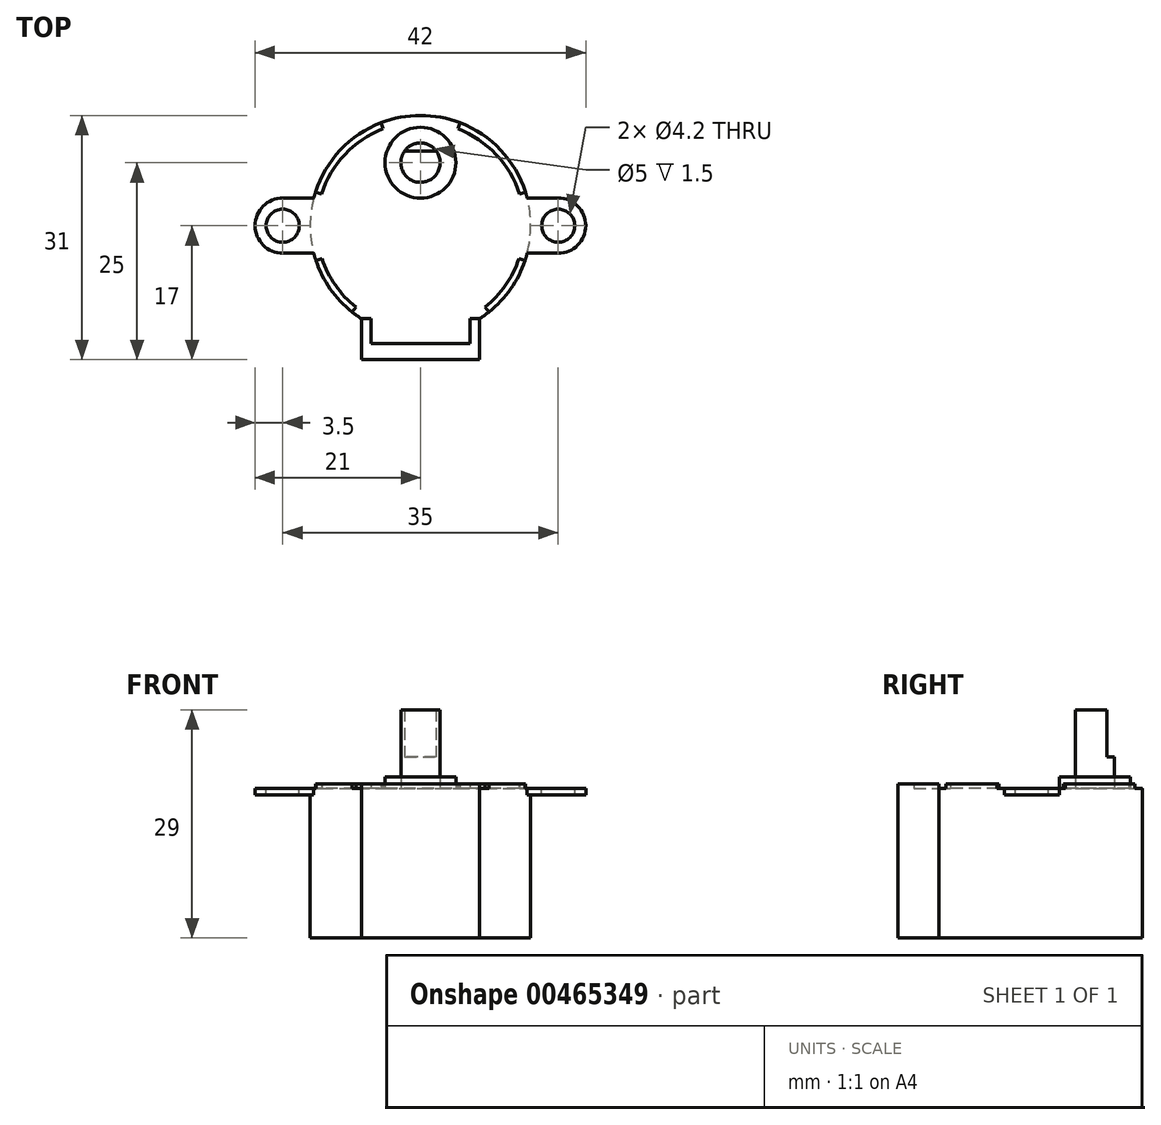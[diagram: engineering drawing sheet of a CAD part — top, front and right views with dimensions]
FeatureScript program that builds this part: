
annotation { "Feature Type Name" : "Feature", "Feature Type Description" : "" }
export const myFeature = defineFeature(function(context is Context, id is Id, definition is map)
    precondition{}
    {
        {
            var Q0;
            Q0=qCreatedBy(makeId("Top.planeOp"),FACE);
            var sketch = newSketch(context, id + "F0", { "sketchPlane" : qUnion([Q0])});
            skArc(sketch, "E0", {"start": v(7.5, -11.82) * mm, "mid": v(0, 14) * mm, "end": v(-7.5, -11.82) * mm});
            skCircle(sketch, "E1", {"center": v(-17.5, 0) * mm, "radius": 2.1 * mm});
            skCircle(sketch, "E2", {"center": v(17.5, 0) * mm, "radius": 2.1 * mm});
            skCircle(sketch, "E3", {"center": v(0, 8) * mm, "radius": 4.5 * mm});
            skArc(sketch, "E4", {"start": v(17.5, -3.5) * mm, "mid": v(21, 0) * mm, "end": v(17.5, 3.5) * mm});
            skArc(sketch, "E5", {"start": v(-17.5, 3.5) * mm, "mid": v(-21, 0) * mm, "end": v(-17.5, -3.5) * mm});
            skLineSegment(sketch, "E6", {"start": v(17.5, -3.5) * mm, "end": v(13.56, -3.5) * mm});
            skLineSegment(sketch, "E7", {"start": v(-17.5, 3.5) * mm, "end": v(-13.56, 3.5) * mm});
            skLineSegment(sketch, "E8.rect.bottom", {"start": v(7.5, -17) * mm, "end": v(-7.5, -17) * mm});
            skLineSegment(sketch, "E8.rect.left", {"start": v(7.5, -17) * mm, "end": v(7.5, -11.82) * mm});
            skLineSegment(sketch, "E8.rect.right", {"start": v(-7.5, -17) * mm, "end": v(-7.5, -11.82) * mm});
            skPoint(sketch, "E9.orphan", {"position": v(-7.5, 17) * mm});
            skPoint(sketch, "E10.orphan", {"position": v(7.5, 17) * mm});
            skLineSegment(sketch, "E11.trimOffspring", {"start": v(13.56, 3.5) * mm, "end": v(17.5, 3.5) * mm});
            skLineSegment(sketch, "E12.trimOffspring", {"start": v(-13.56, -3.5) * mm, "end": v(-17.5, -3.5) * mm});
            skCircle(sketch, "E13", {"center": v(0, 8) * mm, "radius": 2.5 * mm});
            skSolve(sketch);
        }
        {
            var Q0;
            Q0=makeQuery(id+"F0.imprint","IMPRINT",FACE,{"disambiguationData":[TD([[makeQuery(id+"F0.imprint","IMPRINT",EDGE,{"derivedFrom":sQuery(id+"F0.wireOp",EDGE,"E3")}),-1.0]])]});
            var Q1;
            Q1=makeQuery(id+"F0.imprint","IMPRINT",FACE,{"disambiguationData":[TD([[makeQuery(id+"F0.imprint","IMPRINT",EDGE,{"derivedFrom":sQuery(id+"F0.wireOp",EDGE,"E3")}),1.0]])]});
            var Q2;
            Q2=makeQuery(id+"F0.imprint","IMPRINT",FACE,{"disambiguationData":[TD([[makeQuery(id+"F0.imprint","IMPRINT",EDGE,{"derivedFrom":sQuery(id+"F0.wireOp",EDGE,"E13")}),1.0]])]});
            extrude(context, id + "F1", {"entities" : qUnion([Q0, Q1, Q2]), "depth" : 19 * mm});
        }
        {
            var Q0;
            Q0=makeQuery(id+"F0.imprint","IMPRINT",FACE,{"disambiguationData":[TD([[makeQuery(id+"F0.imprint","IMPRINT",EDGE,{"derivedFrom":sQuery(id+"F0.wireOp",EDGE,"E1")}),-1.0]])]});
            var Q1;
            Q1=makeQuery(id+"F0.imprint","IMPRINT",FACE,{"disambiguationData":[TD([[makeQuery(id+"F0.imprint","IMPRINT",EDGE,{"derivedFrom":sQuery(id+"F0.wireOp",EDGE,"E2")}),-1.0]])]});
            extrude(context, id + "F2", {"entities" : qUnion([Q0, Q1]), "operationType" : NewBodyOperationType.ADD, "depth" : 0.8 * mm});
        }
        {
            var Q0;
            Q0=makeQuery(id+"F0.imprint","IMPRINT",FACE,{"disambiguationData":[TD([[makeQuery(id+"F0.imprint","IMPRINT",EDGE,{"derivedFrom":sQuery(id+"F0.wireOp",EDGE,"E3")}),1.0]])]});
            extrude(context, id + "F3", {"entities" : qUnion([Q0]), "operationType" : NewBodyOperationType.ADD, "oppositeDirection" : true, "depth" : 1.5 * mm});
        }
        {
            var Q0;
            Q0=makeQuery(id+"F0.imprint","IMPRINT",FACE,{"disambiguationData":[TD([[makeQuery(id+"F0.imprint","IMPRINT",EDGE,{"derivedFrom":sQuery(id+"F0.wireOp",EDGE,"E13")}),1.0]])]});
            extrude(context, id + "F4", {"entities" : qUnion([Q0]), "oppositeDirection" : true, "depth" : 10 * mm});
        }
        {
            var Q0;
            Q0=makeQuery(id+"F4.opExtrude","CAP_FACE",FACE,{"disambiguationData":[OSD([sQuery(id+"F0.wireOp",EDGE,"E13")])],"isStart":false});
            var sketch = newSketch(context, id + "F5", { "sketchPlane" : qUnion([Q0])});
            skLineSegment(sketch, "E14.rect.bottom", {"start": v(2.91, -9.5) * mm, "end": v(-2.91, -9.5) * mm});
            skLineSegment(sketch, "E14.rect.top", {"start": v(2.91, -6.5) * mm, "end": v(-2.91, -6.5) * mm});
            skLineSegment(sketch, "E14.rect.left", {"start": v(2.91, -9.5) * mm, "end": v(2.91, -6.5) * mm});
            skLineSegment(sketch, "E14.rect.right", {"start": v(-2.91, -9.5) * mm, "end": v(-2.91, -6.5) * mm});
            skPoint(sketch, "E14.rect.middle", {"position": v(0, -8) * mm});
            skLineSegment(sketch, "E15.bottom", {"start": v(-2.91, -6.5) * mm, "end": v(2.91, -6.5) * mm});
            skLineSegment(sketch, "E15.top", {"start": v(-2.91, -5.02) * mm, "end": v(2.91, -5.02) * mm});
            skLineSegment(sketch, "E15.left", {"start": v(-2.91, -6.5) * mm, "end": v(-2.91, -5.02) * mm});
            skLineSegment(sketch, "E15.right", {"start": v(2.91, -6.5) * mm, "end": v(2.91, -5.02) * mm});
            skLineSegment(sketch, "E16.top", {"start": v(2.91, -10.83) * mm, "end": v(-2.91, -10.83) * mm});
            skLineSegment(sketch, "E16.left", {"start": v(2.91, -9.5) * mm, "end": v(2.91, -10.83) * mm});
            skLineSegment(sketch, "E16.right", {"start": v(-2.91, -9.5) * mm, "end": v(-2.91, -10.83) * mm});
            skSolve(sketch);
        }
        {
            var Q0;
            Q0=makeQuery(id+"F5.imprint","IMPRINT",FACE,{"disambiguationData":[TD([[makeQuery(id+"F5.imprint","IMPRINT",EDGE,{"derivedFrom":sQuery(id+"F5.wireOp",EDGE,"E15.top")}),-1.0]])]});
            var Q1;
            {var subQ0=makeQuery(id+"F4.opExtrude","CAP_EDGE",EDGE,{"disambiguationData":[OSD([sQuery(id+"F0.wireOp",EDGE,"E13")])],"isStart":false});var subQ1=sQuery(id+"F5.wireOp",EDGE,"E15.bottom");var subQ3=makeQuery(id+"F5.imprint","INTERSECT",VERTEX,{"disambiguationData":[OD(0.0)],"derivedFrom":[subQ0,subQ1]});Q1=makeQuery(id+"F5.imprint","IMPRINT",FACE,{"disambiguationData":[TD([[makeQuery(id+"F5.imprint","IMPRINT",EDGE,{"disambiguationData":[TD([[subQ3,-1.0]])],"derivedFrom":subQ1}),1.0]])]});}
            var Q2;
            {var subQ0=makeQuery(id+"F4.opExtrude","CAP_EDGE",EDGE,{"disambiguationData":[OSD([sQuery(id+"F0.wireOp",EDGE,"E13")])],"isStart":false});var subQ1=sQuery(id+"F5.wireOp",EDGE,"E14.rect.bottom");var subQ3=makeQuery(id+"F5.imprint","INTERSECT",VERTEX,{"disambiguationData":[OD(0.0)],"derivedFrom":[subQ0,subQ1]});Q2=makeQuery(id+"F5.imprint","IMPRINT",FACE,{"disambiguationData":[TD([[makeQuery(id+"F5.imprint","IMPRINT",EDGE,{"disambiguationData":[TD([[subQ3,-1.0]])],"derivedFrom":subQ1}),1.0]])]});}
            var Q3;
            Q3=makeQuery(id+"F5.imprint","IMPRINT",FACE,{"disambiguationData":[TD([[makeQuery(id+"F5.imprint","IMPRINT",EDGE,{"derivedFrom":sQuery(id+"F5.wireOp",EDGE,"E16.top")}),-1.0]])]});
            extrude(context, id + "F6", {"entities" : qUnion([Q0, Q1, Q2, Q3]), "oppositeDirection" : true, "depth" : 6 * mm});
        }
        {
            var Q0;
            Q0=makeQuery(id+"F6.opExtrude","SWEPT_BODY",BODY,{"disambiguationData":[OSD([sQuery(id+"F5.wireOp",EDGE,"E15.bottom"),sQuery(id+"F5.wireOp",EDGE,"E15.top"),sQuery(id+"F5.wireOp",EDGE,"E15.left"),sQuery(id+"F5.wireOp",EDGE,"E15.right")])]});
            var Q1;
            Q1=makeQuery(id+"F6.opExtrude","SWEPT_BODY",BODY,{"disambiguationData":[OSD([sQuery(id+"F5.wireOp",EDGE,"E14.rect.bottom"),sQuery(id+"F5.wireOp",EDGE,"E16.top"),sQuery(id+"F5.wireOp",EDGE,"E16.left"),sQuery(id+"F5.wireOp",EDGE,"E16.right")])]});
            var Q2;
            Q2=makeQuery(id+"F4.opExtrude","SWEPT_BODY",BODY,{"disambiguationData":[OSD([sQuery(id+"F0.wireOp",EDGE,"E13")])]});
            booleanBodies(context, id + "F7", {"operationType" : BooleanOperationType.SUBTRACTION, "tools" : qUnion([Q0, Q1]), "targets" : qUnion([Q2])});
        }
        {
            var Q0;
            Q0=makeQuery(id+"F0.imprint","IMPRINT",FACE,{"disambiguationData":[TD([[makeQuery(id+"F0.imprint","IMPRINT",EDGE,{"derivedFrom":sQuery(id+"F0.wireOp",EDGE,"E3")}),-1.0]])]});
            var sketch = newSketch(context, id + "F8", { "sketchPlane" : qUnion([Q0])});
            skArc(sketch, "E17", {"start": v(-12.51, -4.2) * mm, "mid": v(-10.8, -7.58) * mm, "end": v(-8.22, -10.33) * mm});
            skArc(sketch, "E18", {"start": v(-13.27, -4.45) * mm, "mid": v(-11.46, -8.04) * mm, "end": v(-8.71, -10.96) * mm});
            skLineSegment(sketch, "E19", {"start": v(-8.71, -10.96) * mm, "end": v(-8.22, -10.33) * mm});
            skLineSegment(sketch, "E20", {"start": v(-13.27, -4.45) * mm, "end": v(-12.51, -4.2) * mm});
            skLineSegment(sketch, "E21", {"start": v(-12.58, 4) * mm, "end": v(-13.34, 4.25) * mm});
            skLineSegment(sketch, "E22", {"start": v(-4.75, 12.32) * mm, "end": v(-5.04, 13.06) * mm});
            skLineSegment(sketch, "E23.MirrorCS", {"start": v(4.75, 12.32) * mm, "end": v(5.04, 13.06) * mm});
            skLineSegment(sketch, "E24.MirrorCS", {"start": v(12.58, 4) * mm, "end": v(13.34, 4.25) * mm});
            skLineSegment(sketch, "E25.MirrorCS", {"start": v(8.71, -10.96) * mm, "end": v(8.22, -10.33) * mm});
            skLineSegment(sketch, "E26.MirrorCS", {"start": v(13.27, -4.45) * mm, "end": v(12.51, -4.2) * mm});
            skArc(sketch, "E27.trimOffspring", {"start": v(8.71, -10.96) * mm, "mid": v(11.46, -8.04) * mm, "end": v(13.27, -4.45) * mm});
            skArc(sketch, "E28.trimOffspring", {"start": v(8.22, -10.33) * mm, "mid": v(10.8, -7.58) * mm, "end": v(12.51, -4.2) * mm});
            skArc(sketch, "E29.trimOffspring", {"start": v(13.34, 4.25) * mm, "mid": v(10.2, 9.6) * mm, "end": v(5.04, 13.06) * mm});
            skArc(sketch, "E30.trimOffspring", {"start": v(12.58, 4) * mm, "mid": v(9.6, 9.05) * mm, "end": v(4.75, 12.32) * mm});
            skArc(sketch, "E31.trimOffspring", {"start": v(-4.75, 12.32) * mm, "mid": v(-9.6, 9.05) * mm, "end": v(-12.58, 4) * mm});
            skArc(sketch, "E32.trimOffspring", {"start": v(-5.04, 13.06) * mm, "mid": v(-10.2, 9.6) * mm, "end": v(-13.34, 4.25) * mm});
            skLineSegment(sketch, "E33", {"start": v(-6.3, -15) * mm, "end": v(6.3, -15) * mm});
            skLineSegment(sketch, "E34", {"start": v(6.3, -15) * mm, "end": v(6.3, -11.82) * mm});
            skLineSegment(sketch, "E35", {"start": v(6.3, -11.82) * mm, "end": v(7.5, -11.82) * mm});
            skLineSegment(sketch, "E36", {"start": v(7.5, -11.82) * mm, "end": v(7.5, -17) * mm});
            skLineSegment(sketch, "E37", {"start": v(7.5, -17) * mm, "end": v(-7.5, -17) * mm});
            skLineSegment(sketch, "E38", {"start": v(-7.5, -17) * mm, "end": v(-7.5, -11.82) * mm});
            skLineSegment(sketch, "E39", {"start": v(-7.5, -11.82) * mm, "end": v(-6.3, -11.82) * mm});
            skLineSegment(sketch, "E40", {"start": v(-6.3, -11.82) * mm, "end": v(-6.3, -15) * mm});
            skSolve(sketch);
        }
        {
            var Q0;
            Q0=qSketchRegion(id+"F8",true);
            extrude(context, id + "F9", {"entities" : qUnion([Q0]), "operationType" : NewBodyOperationType.ADD, "oppositeDirection" : true, "depth" : 0.6 * mm});
        }
        {
            var Q0;
            Q0=makeQuery(id+"F1.opExtrude","SWEPT_BODY",BODY,{"disambiguationData":[OSD([sQuery(id+"F0.wireOp",EDGE,"E0"),sQuery(id+"F0.wireOp",EDGE,"E8.rect.bottom"),sQuery(id+"F0.wireOp",EDGE,"E8.rect.left"),sQuery(id+"F0.wireOp",EDGE,"E8.rect.right")])]});
            var Q1;
            Q1=makeQuery(id+"F4.opExtrude","SWEPT_BODY",BODY,{"disambiguationData":[OSD([sQuery(id+"F0.wireOp",EDGE,"E13")])]});
            var Q2;
            Q2=makeQuery(id+"F9.opExtrude","CAP_EDGE",EDGE,{"disambiguationData":[OSD([sQuery(id+"F8.wireOp",EDGE,"E36")])],"isStart":false});
            transform(context, id + "F10", {"entities" : qUnion([Q0, Q1]), "transformType" : TransformType.ROTATION, "transformAxis" : qUnion([Q2]), "angle" : 180 * degree, "makeCopy" : false});
        }
    });
